# Revit family: Sanitary_Basins_LAUFEN_KbL-600-mm-Washbasin_
name_source: partatom
category: Plumbing Fixtures
revit_build: Autodesk Revit 2015 (Build: 20140903_1530(x64)
units: mm (PartAtom-declared; Revit-internal decimal feet)

## types (1)
- Default
    BIMobject category = Basins
    BIMobject category code = sanitary-basins
    BIMobject main category = Sanitary
    BIMobject main category code = sanitary
    BOSUseNativeGeometries = 1
    Brand url = http://www.laufen.com
    Design country = Switzerland
    Edition number = 1
    IFC Classification = Sanitary Terminal
    Manufacturer country = Austria
    Manufacturer name = LAUFEN
    Masterformat 2014 Code = 22 41 16.16
    Masterformat 2014 Description = Residential Sinks
    Material main = SaphirKeramik
    NBS Reference Code = 35-65-70-94
    NBS Reference Description = Wash Basin Systems
    Nominal height = 145
    Nominal width = 600
    OmniClass Code = 23-31 13 00
    OmniClass Description = Sinks
    Product Guid = 0b66ec8a-20a2-44b6-930c-aa0b50656ba8
    Product SKU = 810333
    Product certification = http://www.export.laufen.com
    Product data url = https://bimobject.com
    Product family = Kartell by Laufen
    Product group = BASINS
    Product name = KbL 600 mm Washbasin
    Product url = http://www.export.laufen.com
    QR code = http://bimobject.com
    UNSPSC Code = 30181504
    Uniclass 1.4 Code = L7212
    Uniclass 1.4 Description = Washbasins
    Uniclass 2.0 Code = SS-35-65-70-94
    Uniclass 2.0 Description = Wash Basin Systems
    Uniclass 2015 Code = Ss_40_15_75_94
    Uniclass 2015 Name = Wash basin systems
    Uniformat II Code = D2010
    Uniformat II Description = Plumbing Fixtures
    Weight Net (Kg) = 14.1

## geometry (parser evidence)
native form markers: Sweep x4
no freeform markers — native parametric forms only
